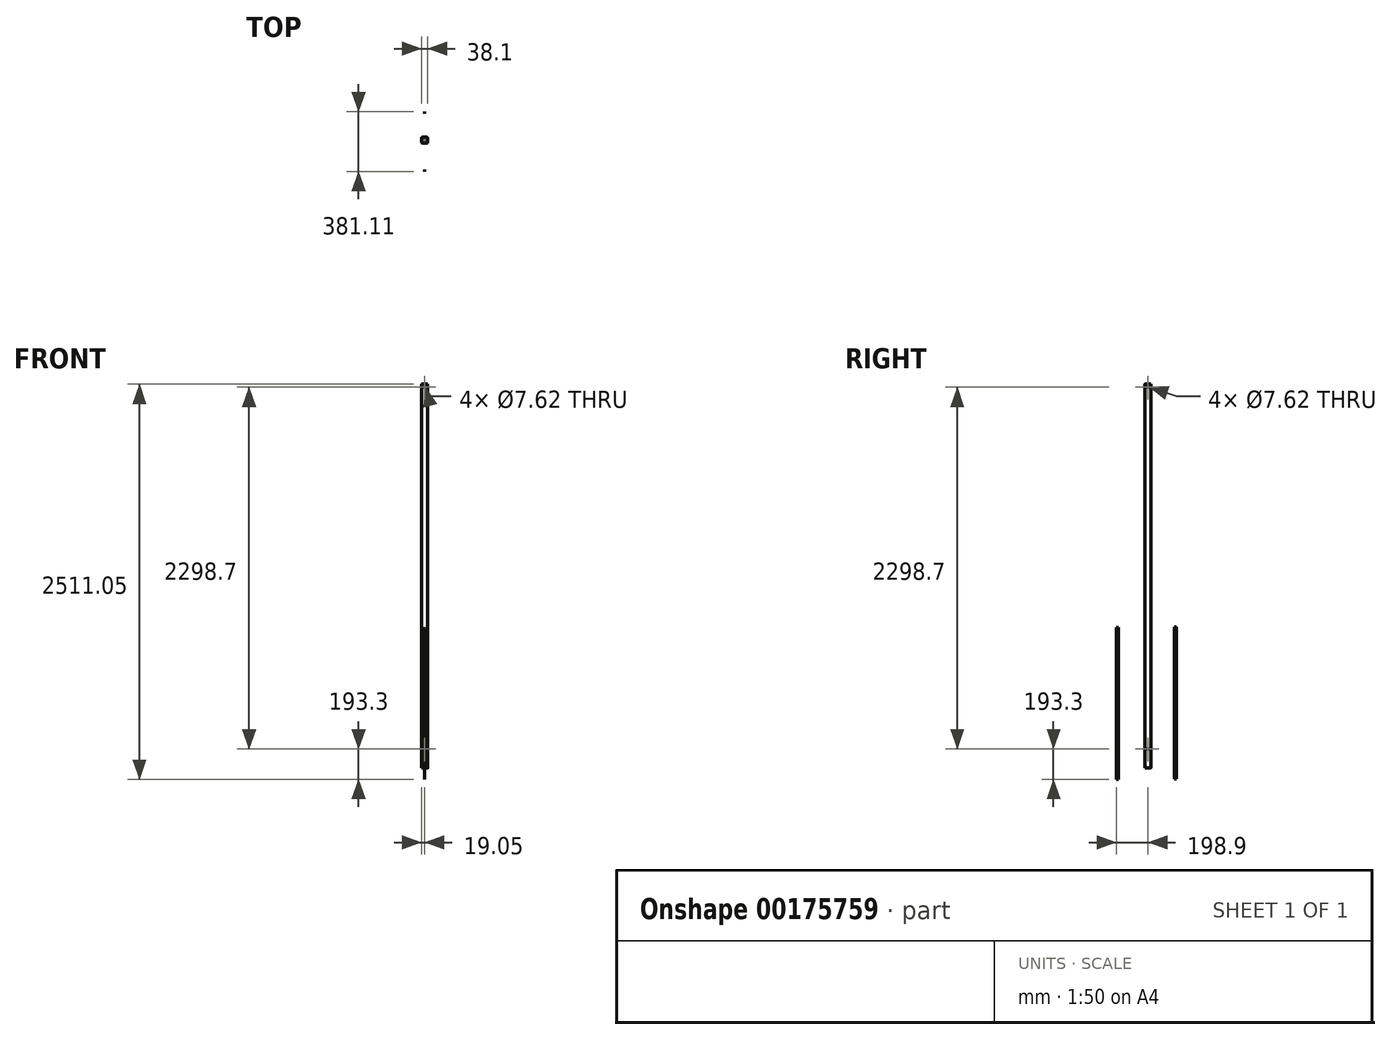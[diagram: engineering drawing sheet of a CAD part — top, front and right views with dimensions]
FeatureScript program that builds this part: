
annotation { "Feature Type Name" : "Feature", "Feature Type Description" : "" }
export const myFeature = defineFeature(function(context is Context, id is Id, definition is map)
    precondition{}
    {
        {
            var Q0;
            Q0=qCreatedBy(makeId("Top.planeOp"),FACE);
            var sketch = newSketch(context, id + "F0", { "sketchPlane" : qUnion([Q0])});
            skLineSegment(sketch, "E0.bottom", {"start": v(12.7, 19.05) * mm, "end": v(-12.7, 19.05) * mm});
            skLineSegment(sketch, "E0.top", {"start": v(12.7, -19.05) * mm, "end": v(-12.7, -19.05) * mm});
            skLineSegment(sketch, "E0.left", {"start": v(19.05, 12.7) * mm, "end": v(19.05, -12.7) * mm});
            skLineSegment(sketch, "E0.right", {"start": v(-19.05, 12.7) * mm, "end": v(-19.05, -12.7) * mm});
            skPoint(sketch, "E0.middle", {"position": v(0, 0) * mm});
            skPoint(sketch, "E1.visualSharp", {"position": v(-19.05, 19.05) * mm});
            skArc(sketch, "E1.filletArc", {"start": v(-12.7, 19.05) * mm, "mid": v(-17.2, 17.2) * mm, "end": v(-19.05, 12.7) * mm});
            skPoint(sketch, "E2.visualSharp", {"position": v(19.05, 19.05) * mm});
            skArc(sketch, "E2.filletArc", {"start": v(19.05, 12.7) * mm, "mid": v(17.2, 17.2) * mm, "end": v(12.7, 19.05) * mm});
            skPoint(sketch, "E3.visualSharp", {"position": v(19.05, -19.05) * mm});
            skArc(sketch, "E3.filletArc", {"start": v(12.7, -19.05) * mm, "mid": v(17.2, -17.2) * mm, "end": v(19.05, -12.7) * mm});
            skPoint(sketch, "E4.visualSharp", {"position": v(-19.05, -19.05) * mm});
            skArc(sketch, "E4.filletArc", {"start": v(-19.05, -12.7) * mm, "mid": v(-17.2, -17.2) * mm, "end": v(-12.7, -19.05) * mm});
            skSolve(sketch);
        }
        {
            var Q0;
            Q0=qSketchRegion(id+"F0",true);
            extrude(context, id + "F1", {"entities" : qUnion([Q0]), "depth" : 2438.4 * mm});
        }
        {
            var Q0;
            Q0=qCreatedBy(makeId("Right.planeOp"),FACE);
            var sketch = newSketch(context, id + "F2", { "sketchPlane" : qUnion([Q0])});
            skLineSegment(sketch, "E5.bottom", {"start": v(-186.2, -72.65) * mm, "end": v(-198.9, -72.65) * mm});
            skLineSegment(sketch, "E5.top", {"start": v(-186.2, 892.55) * mm, "end": v(-198.9, 892.55) * mm});
            skLineSegment(sketch, "E5.left", {"start": v(-186.2, -72.65) * mm, "end": v(-186.2, 892.55) * mm});
            skLineSegment(sketch, "E5.right", {"start": v(-198.9, -72.65) * mm, "end": v(-198.9, 892.55) * mm});
            skPoint(sketch, "E5.middle", {"position": v(-192.55, 409.95) * mm});
            skSolve(sketch);
        }
        {
            var Q0;
            Q0=qCreatedBy(makeId("Right.planeOp"),FACE);
            var sketch = newSketch(context, id + "F3", { "sketchPlane" : qUnion([Q0])});
            skLineSegment(sketch, "E6.bottom", {"start": v(182.21, -70.47) * mm, "end": v(169.51, -70.47) * mm});
            skLineSegment(sketch, "E6.top", {"start": v(182.21, 894.73) * mm, "end": v(169.51, 894.73) * mm});
            skLineSegment(sketch, "E6.left", {"start": v(182.21, -70.47) * mm, "end": v(182.21, 894.73) * mm});
            skLineSegment(sketch, "E6.right", {"start": v(169.51, -70.47) * mm, "end": v(169.51, 894.73) * mm});
            skPoint(sketch, "E6.middle", {"position": v(175.86, 412.13) * mm});
            skSolve(sketch);
        }
        {
            var Q0;
            Q0=makeQuery(id+"F2.imprint","IMPRINT",FACE,{"disambiguationData":[TD([[makeQuery(id+"F2.imprint","IMPRINT",EDGE,{"derivedFrom":sQuery(id+"F2.wireOp",EDGE,"E5.bottom")}),-1.0]])]});
            extrude(context, id + "F4", {"entities" : qUnion([Q0]), "depth" : 0.25 * mm});
        }
        {
            var Q0;
            Q0=makeQuery(id+"F3.imprint","IMPRINT",FACE,{"disambiguationData":[TD([[makeQuery(id+"F3.imprint","IMPRINT",EDGE,{"derivedFrom":sQuery(id+"F3.wireOp",EDGE,"E6.bottom")}),-1.0]])]});
            extrude(context, id + "F5", {"entities" : qUnion([Q0]), "depth" : 0.25 * mm});
        }
        {
            var Q0;
            Q0=makeQuery(id+"F1.opExtrude","SWEPT_FACE",FACE,{"disambiguationData":[OSD([sQuery(id+"F0.wireOp",EDGE,"E0.top")])]});
            var sketch = newSketch(context, id + "F6", { "sketchPlane" : qUnion([Q0])});
            skLineSegment(sketch, "E7", {"start": v(0, 0) * mm, "end": v(0, 120.65) * mm});
            skCircle(sketch, "E8", {"center": v(0, 120.65) * mm, "radius": 3.81 * mm});
            skSolve(sketch);
        }
        {
            var Q0;
            Q0 = qSketchRegion(id + "F6", true);
            extrude(context, id + "F7", {"entities" : qUnion([Q0]), "operationType" : NewBodyOperationType.REMOVE, "oppositeDirection" : true, "depth" : 38.1 * mm});
        }
        {
            var Q0;
            Q0=makeQuery(id+"F1.opExtrude","SWEPT_FACE",FACE,{"disambiguationData":[OSD([sQuery(id+"F0.wireOp",EDGE,"E0.left")])]});
            var sketch = newSketch(context, id + "F8", { "sketchPlane" : qUnion([Q0])});
            skLineSegment(sketch, "E9", {"start": v(0, 0) * mm, "end": v(0, 120.65) * mm});
            skPoint(sketch, "E9.endSnap0", {"position": v(0, 0) * mm});
            skCircle(sketch, "E10", {"center": v(0, 120.65) * mm, "radius": 3.81 * mm});
            skSolve(sketch);
        }
        {
            var Q0;
            Q0 = qSketchRegion(id + "F8", true);
            extrude(context, id + "F9", {"entities" : qUnion([Q0]), "operationType" : NewBodyOperationType.REMOVE, "oppositeDirection" : true, "depth" : 38.1 * mm});
        }
        {
            var Q0;
            Q0=makeQuery(id+"F1.opExtrude","SWEPT_FACE",FACE,{"disambiguationData":[OSD([sQuery(id+"F0.wireOp",EDGE,"E0.top")])]});
            var sketch = newSketch(context, id + "F10", { "sketchPlane" : qUnion([Q0])});
            skLineSegment(sketch, "E11", {"start": v(0, 2438.4) * mm, "end": v(0, 2419.35) * mm});
            skPoint(sketch, "E11.endSnap0", {"position": v(0, 2438.4) * mm});
            skCircle(sketch, "E12", {"center": v(0, 2419.35) * mm, "radius": 3.81 * mm});
            skSolve(sketch);
        }
        {
            var Q0;
            Q0 = qSketchRegion(id + "F10", true);
            extrude(context, id + "F11", {"entities" : qUnion([Q0]), "operationType" : NewBodyOperationType.REMOVE, "oppositeDirection" : true, "depth" : 38.1 * mm});
        }
        {
            var Q0;
            Q0=makeQuery(id+"F1.opExtrude","SWEPT_FACE",FACE,{"disambiguationData":[OSD([sQuery(id+"F0.wireOp",EDGE,"E0.left")])]});
            var sketch = newSketch(context, id + "F12", { "sketchPlane" : qUnion([Q0])});
            skLineSegment(sketch, "E13", {"start": v(0, 2438.4) * mm, "end": v(0, 2419.35) * mm});
            skPoint(sketch, "E13.endSnap0", {"position": v(0, 2438.4) * mm});
            skCircle(sketch, "E14", {"center": v(0, 2419.35) * mm, "radius": 3.81 * mm});
            skSolve(sketch);
        }
        {
            var Q0;
            Q0 = qSketchRegion(id + "F12", true);
            extrude(context, id + "F13", {"entities" : qUnion([Q0]), "operationType" : NewBodyOperationType.REMOVE, "oppositeDirection" : true, "depth" : 38.1 * mm});
        }
    });
